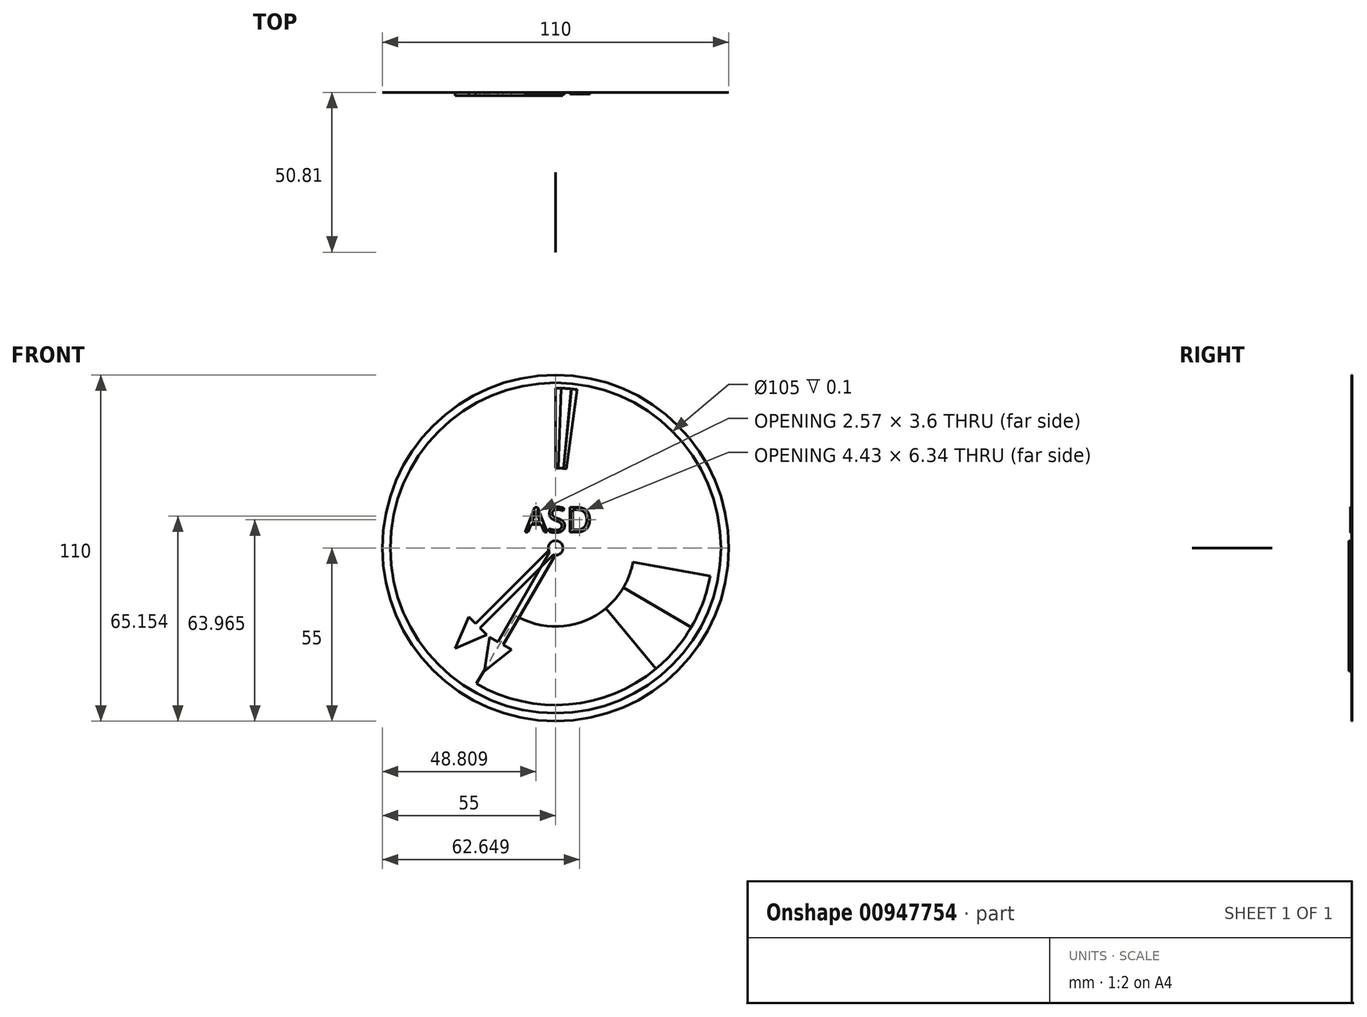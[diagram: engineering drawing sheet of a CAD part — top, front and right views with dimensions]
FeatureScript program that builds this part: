
annotation { "Feature Type Name" : "Feature", "Feature Type Description" : "" }
export const myFeature = defineFeature(function(context is Context, id is Id, definition is map)
    precondition{}
    {
        {
            var Q0;
            Q0=qCreatedBy(makeId("Right.planeOp"),FACE);
            var sketch = newSketch(context, id + "F0", { "sketchPlane" : qUnion([Q0])});
            skLineSegment(sketch, "E0", {"start": v(0, 0) * mm, "end": v(-116.06, 0) * mm, "construction": true});
            skSolve(sketch);
        }
        {
            var Q0;
            Q0=qCreatedBy(makeId("Right.planeOp"),FACE);
            var Q1;
            Q1=sQuery(id+"F0.wireOp",EDGE,"E0");
            cPlane(context, id + "F1", {"entities" : qUnion([Q0, Q1]), "cplaneType" : CPlaneType.LINE_ANGLE, "offset" : 25 * mm, "angle" : 135 * degree, "width" : 150 * mm, "height" : 150 * mm});
        }
        {
            var Q0;
            Q0=qCreatedBy(id+"F1.planeOp",FACE);
            var sketch = newSketch(context, id + "F2", { "sketchPlane" : qUnion([Q0])});
            skLineSegment(sketch, "E1.bottom", {"start": v(-25.4, 0) * mm, "end": v(-50.8, 0) * mm});
            skLineSegment(sketch, "E1.top", {"start": v(-25.4, 0) * mm, "end": v(-50.8, 0) * mm});
            skLineSegment(sketch, "E1.left", {"start": v(-25.4, 0) * mm, "end": v(-25.4, 0) * mm});
            skLineSegment(sketch, "E1.right", {"start": v(-50.8, 0) * mm, "end": v(-50.8, 0) * mm});
            skSolve(sketch);
        }
        {
            var Q0;
            Q0=qSketchRegion(id+"F2",true);
            var Q1;
            Q1=sQuery(id+"F0.wireOp",EDGE,"E0");
            revolve(context, id + "F3", {"surfaceOperationType" : NewSurfaceOperationType.NEW, "entities" : qUnion([Q0]), "axis" : qUnion([Q1]), "revolveType" : RevolveType.ONE_DIRECTION, "oppositeDirection" : true, "angle" : 135 * degree});
        }
        {
            var Q0;
            Q0=qCreatedBy(makeId("Right.planeOp"),FACE);
            var sketch = newSketch(context, id + "F4", { "sketchPlane" : qUnion([Q0])});
            skLineSegment(sketch, "E2.bottom", {"start": v(-0.01, 50.8) * mm, "end": v(0, 50.8) * mm});
            skLineSegment(sketch, "E2.top", {"start": v(0, 25.4) * mm, "end": v(0, 25.4) * mm});
            skLineSegment(sketch, "E2.left", {"start": v(-0.01, 50.8) * mm, "end": v(0, 25.4) * mm});
            skLineSegment(sketch, "E2.right", {"start": v(0, 50.8) * mm, "end": v(0, 25.4) * mm});
            skSolve(sketch);
        }
        {
            var Q0;
            Q0=qSketchRegion(id+"F4",true);
            var Q1;
            Q1=sQuery(id+"F0.wireOp",EDGE,"E0");
            revolve(context, id + "F5", {"surfaceOperationType" : NewSurfaceOperationType.NEW, "entities" : qUnion([Q0]), "axis" : qUnion([Q1]), "revolveType" : RevolveType.ONE_DIRECTION, "oppositeDirection" : true, "angle" : 2 * degree});
        }
        {
            var Q0;
            Q0=qCreatedBy(makeId("Right.planeOp"),FACE);
            var Q1;
            Q1=sQuery(id+"F0.wireOp",EDGE,"E0");
            cPlane(context, id + "F6", {"entities" : qUnion([Q0, Q1]), "cplaneType" : CPlaneType.LINE_ANGLE, "offset" : 25 * mm, "angle" : 2 * degree, "oppositeDirection" : true, "width" : 150 * mm, "height" : 150 * mm});
        }
        {
            var Q0;
            Q0=qCreatedBy(id+"F6.planeOp",FACE);
            var sketch = newSketch(context, id + "F7", { "sketchPlane" : qUnion([Q0])});
            skLineSegment(sketch, "E3.bottom", {"start": v(0, 50.8) * mm, "end": v(0, 50.8) * mm});
            skLineSegment(sketch, "E3.top", {"start": v(0, 25.4) * mm, "end": v(0, 25.4) * mm});
            skLineSegment(sketch, "E3.left", {"start": v(0, 50.8) * mm, "end": v(0, 25.4) * mm});
            skLineSegment(sketch, "E3.right", {"start": v(0, 50.8) * mm, "end": v(0, 25.4) * mm});
            skSolve(sketch);
        }
        {
            var Q0;
            Q0=qSketchRegion(id+"F7",true);
            var Q1;
            Q1=sQuery(id+"F0.wireOp",EDGE,"E0");
            revolve(context, id + "F8", {"surfaceOperationType" : NewSurfaceOperationType.NEW, "entities" : qUnion([Q0]), "axis" : qUnion([Q1]), "revolveType" : RevolveType.ONE_DIRECTION, "oppositeDirection" : true, "angle" : 3.6 * degree});
        }
        {
            var Q0;
            Q0=qCreatedBy(makeId("Front.planeOp"),FACE);
            var sketch = newSketch(context, id + "F9", { "sketchPlane" : qUnion([Q0])});
            skLineSegment(sketch, "E4.bottom", {"start": v(-0.77, -2.19) * mm, "end": v(-24.04, -25.46) * mm});
            skLineSegment(sketch, "E4.top", {"start": v(-2.19, -0.77) * mm, "end": v(-25.46, -24.04) * mm});
            skPoint(sketch, "E4.middle", {"position": v(0, 0) * mm});
            skLineSegment(sketch, "E5", {"start": v(0, 0) * mm, "end": v(0, 10.99) * mm, "construction": true});
            skPoint(sketch, "E6", {"position": v(-24.75, -24.75) * mm});
            skCircle(sketch, "E7", {"center": v(-24.75, -24.75) * mm, "radius": 10.19 * mm, "construction": true});
            skLineSegment(sketch, "E8", {"start": v(-24.04, -25.46) * mm, "end": v(-21.92, -27.58) * mm});
            skLineSegment(sketch, "E9", {"start": v(-25.46, -24.04) * mm, "end": v(-27.58, -21.92) * mm});
            skLineSegment(sketch, "E10", {"start": v(-24.75, -24.75) * mm, "end": v(-31.95, -31.95) * mm, "construction": true});
            skLineSegment(sketch, "E11", {"start": v(-31.95, -31.95) * mm, "end": v(-27.58, -21.92) * mm});
            skLineSegment(sketch, "E12", {"start": v(-21.92, -27.58) * mm, "end": v(-31.95, -31.95) * mm});
            skArc(sketch, "E13", {"start": v(-0.77, -2.19) * mm, "mid": v(1.64, 1.64) * mm, "end": v(-2.19, -0.77) * mm});
            skPoint(sketch, "E14.orphan", {"position": v(-0.7, 0.7) * mm});
            skPoint(sketch, "E15.end.orphan", {"position": v(0.7, -0.7) * mm});
            skSolve(sketch);
        }
        {
            var Q0;
            Q0=qSketchRegion(id+"F9",true);
            extrude(context, id + "F10", {"entities" : qUnion([Q0]), "depth" : 1 * mm, "offsetDistance" : 25 * mm});
        }
        {
            var Q0;
            Q0=qCreatedBy(makeId("Front.planeOp"),FACE);
            var sketch = newSketch(context, id + "F11", { "sketchPlane" : qUnion([Q0])});
            skCircle(sketch, "E16", {"center": v(0, 0) * mm, "radius": 52.5 * mm});
            skCircle(sketch, "E17", {"center": v(0, 0) * mm, "radius": 55 * mm});
            skSolve(sketch);
        }
        {
            var Q0;
            Q0=qSketchRegion(id+"F11",true);
            extrude(context, id + "F12", {"entities" : qUnion([Q0]), "depth" : .1 * mm, "offsetDistance" : 25 * mm});
        }
        {
            var Q0;
            Q0=qCreatedBy(makeId("Front.planeOp"),FACE);
            var sketch = newSketch(context, id + "F13", { "sketchPlane" : qUnion([Q0])});
            skPoint(sketch, "E18.middle", {"position": v(68.26, -76.77) * mm});
            skText(sketch, "E19", { "text": "SPEED", "fontName": "OpenSans-Bold.ttf"});
            skLineSegment(sketch, "E20", {"start": v(0, 0) * mm, "end": v(0, -24.7) * mm, "construction": true});
            const initialGuessF13  = {"E19": [-0.015, -0.03702, 1, 0, 0.007]};
            skSetInitialGuess(sketch, initialGuessF13);
            skSolve(sketch);
        }
        {
            var Q0;
            Q0 = qSketchRegion(id + "F13", true);
            extrude(context, id + "F14", {"entities" : qUnion([Q0]), "depth" : .1 * mm, "offsetDistance" : 25 * mm});
        }
        {
            var Q0;
            Q0=qCreatedBy(makeId("Front.planeOp"),FACE);
            var sketch = newSketch(context, id + "F15", { "sketchPlane" : qUnion([Q0])});
            skLineSegment(sketch, "E21", {"start": v(3.53, 25.15) * mm, "end": v(7.07, 50.3) * mm});
            skLineSegment(sketch, "E22", {"start": v(0, 0) * mm, "end": v(0, 18.46) * mm, "construction": true});
            skArc(sketch, "E23", {"start": v(3.53, 25.15) * mm, "mid": v(3.97, 25.09) * mm, "end": v(4.41, 25.01) * mm});
            skArc(sketch, "E24", {"start": v(7.07, 50.3) * mm, "mid": v(7.95, 50.17) * mm, "end": v(8.82, 50.03) * mm});
            skLineSegment(sketch, "E25", {"start": v(4.41, 25.01) * mm, "end": v(8.82, 50.03) * mm});
            skSolve(sketch);
        }
        {
            var Q0;
            Q0 = qSketchRegion(id + "F15", true);
            extrude(context, id + "F16", {"entities" : qUnion([Q0]), "depth" : .1 * mm, "offsetDistance" : 25 * mm});
        }
        {
            var Q0;
            Q0=makeQuery(id+"F16.opExtrude","SWEPT_BODY",BODY,{"disambiguationData":[OSD([sQuery(id+"F15.wireOp",EDGE,"E21"),sQuery(id+"F15.wireOp",EDGE,"E23"),sQuery(id+"F15.wireOp",EDGE,"E24"),sQuery(id+"F15.wireOp",EDGE,"E25")])]});
            var Q1;
            Q1=makeQuery(id+"F12.opExtrude","CAP_EDGE",EDGE,{"disambiguationData":[OSD([sQuery(id+"F11.wireOp",EDGE,"E16")])],"isStart":false});
            transform(context, id + "F17", {"entities" : qUnion([Q0]), "transformType" : TransformType.ROTATION, "transformAxis" : qUnion([Q1]), "angle" : 2.3 * degree, "makeCopy" : false});
        }
        {
            var Q0;
            Q0=makeQuery(id+"F14.opExtrude","SWEPT_BODY",BODY,{"disambiguationData":[OSD([sQuery(id+"F13.wireOp",EDGE,"E19.sketch_text.stroke-0"),sQuery(id+"F13.wireOp",EDGE,"E19.sketch_text.stroke-1"),sQuery(id+"F13.wireOp",EDGE,"E19.sketch_text.stroke-2"),sQuery(id+"F13.wireOp",EDGE,"E19.sketch_text.stroke-3"),sQuery(id+"F13.wireOp",EDGE,"E19.sketch_text.stroke-4"),sQuery(id+"F13.wireOp",EDGE,"E19.sketch_text.stroke-5"),sQuery(id+"F13.wireOp",EDGE,"E19.sketch_text.stroke-6"),sQuery(id+"F13.wireOp",EDGE,"E19.sketch_text.stroke-7"),sQuery(id+"F13.wireOp",EDGE,"E19.sketch_text.stroke-8"),sQuery(id+"F13.wireOp",EDGE,"E19.sketch_text.stroke-9"),sQuery(id+"F13.wireOp",EDGE,"E19.sketch_text.stroke-10"),sQuery(id+"F13.wireOp",EDGE,"E19.sketch_text.stroke-11"),sQuery(id+"F13.wireOp",EDGE,"E19.sketch_text.stroke-12"),sQuery(id+"F13.wireOp",EDGE,"E19.sketch_text.stroke-13"),sQuery(id+"F13.wireOp",EDGE,"E19.sketch_text.stroke-14"),sQuery(id+"F13.wireOp",EDGE,"E19.sketch_text.stroke-15"),sQuery(id+"F13.wireOp",EDGE,"E19.sketch_text.stroke-16"),sQuery(id+"F13.wireOp",EDGE,"E19.sketch_text.stroke-17"),sQuery(id+"F13.wireOp",EDGE,"E19.sketch_text.stroke-18"),sQuery(id+"F13.wireOp",EDGE,"E19.sketch_text.stroke-19"),sQuery(id+"F13.wireOp",EDGE,"E19.sketch_text.stroke-20"),sQuery(id+"F13.wireOp",EDGE,"E19.sketch_text.stroke-21"),sQuery(id+"F13.wireOp",EDGE,"E19.sketch_text.stroke-22"),sQuery(id+"F13.wireOp",EDGE,"E19.sketch_text.stroke-23"),sQuery(id+"F13.wireOp",EDGE,"E19.sketch_text.stroke-24"),sQuery(id+"F13.wireOp",EDGE,"E19.sketch_text.stroke-25"),sQuery(id+"F13.wireOp",EDGE,"E19.sketch_text.stroke-26"),sQuery(id+"F13.wireOp",EDGE,"E19.sketch_text.stroke-27")])]});
            var Q1;
            Q1=makeQuery(id+"F14.opExtrude","SWEPT_BODY",BODY,{"disambiguationData":[OSD([sQuery(id+"F13.wireOp",EDGE,"E19.sketch_text.stroke-28"),sQuery(id+"F13.wireOp",EDGE,"E19.sketch_text.stroke-29"),sQuery(id+"F13.wireOp",EDGE,"E19.sketch_text.stroke-30"),sQuery(id+"F13.wireOp",EDGE,"E19.sketch_text.stroke-31"),sQuery(id+"F13.wireOp",EDGE,"E19.sketch_text.stroke-32"),sQuery(id+"F13.wireOp",EDGE,"E19.sketch_text.stroke-33"),sQuery(id+"F13.wireOp",EDGE,"E19.sketch_text.stroke-34"),sQuery(id+"F13.wireOp",EDGE,"E19.sketch_text.stroke-35"),sQuery(id+"F13.wireOp",EDGE,"E19.sketch_text.stroke-36"),sQuery(id+"F13.wireOp",EDGE,"E19.sketch_text.stroke-37"),sQuery(id+"F13.wireOp",EDGE,"E19.sketch_text.stroke-38"),sQuery(id+"F13.wireOp",EDGE,"E19.sketch_text.stroke-39"),sQuery(id+"F13.wireOp",EDGE,"E19.sketch_text.stroke-40"),sQuery(id+"F13.wireOp",EDGE,"E19.sketch_text.stroke-41"),sQuery(id+"F13.wireOp",EDGE,"E19.sketch_text.stroke-42"),sQuery(id+"F13.wireOp",EDGE,"E19.sketch_text.stroke-43")])]});
            var Q2;
            Q2=makeQuery(id+"F14.opExtrude","SWEPT_BODY",BODY,{"disambiguationData":[OSD([sQuery(id+"F13.wireOp",EDGE,"E19.sketch_text.stroke-44"),sQuery(id+"F13.wireOp",EDGE,"E19.sketch_text.stroke-45"),sQuery(id+"F13.wireOp",EDGE,"E19.sketch_text.stroke-46"),sQuery(id+"F13.wireOp",EDGE,"E19.sketch_text.stroke-47"),sQuery(id+"F13.wireOp",EDGE,"E19.sketch_text.stroke-48"),sQuery(id+"F13.wireOp",EDGE,"E19.sketch_text.stroke-49"),sQuery(id+"F13.wireOp",EDGE,"E19.sketch_text.stroke-50"),sQuery(id+"F13.wireOp",EDGE,"E19.sketch_text.stroke-51"),sQuery(id+"F13.wireOp",EDGE,"E19.sketch_text.stroke-52"),sQuery(id+"F13.wireOp",EDGE,"E19.sketch_text.stroke-53"),sQuery(id+"F13.wireOp",EDGE,"E19.sketch_text.stroke-54"),sQuery(id+"F13.wireOp",EDGE,"E19.sketch_text.stroke-55")])]});
            var Q3;
            Q3=makeQuery(id+"F14.opExtrude","SWEPT_BODY",BODY,{"disambiguationData":[OSD([sQuery(id+"F13.wireOp",EDGE,"E19.sketch_text.stroke-56"),sQuery(id+"F13.wireOp",EDGE,"E19.sketch_text.stroke-57"),sQuery(id+"F13.wireOp",EDGE,"E19.sketch_text.stroke-58"),sQuery(id+"F13.wireOp",EDGE,"E19.sketch_text.stroke-59"),sQuery(id+"F13.wireOp",EDGE,"E19.sketch_text.stroke-60"),sQuery(id+"F13.wireOp",EDGE,"E19.sketch_text.stroke-61"),sQuery(id+"F13.wireOp",EDGE,"E19.sketch_text.stroke-62"),sQuery(id+"F13.wireOp",EDGE,"E19.sketch_text.stroke-63"),sQuery(id+"F13.wireOp",EDGE,"E19.sketch_text.stroke-64"),sQuery(id+"F13.wireOp",EDGE,"E19.sketch_text.stroke-65"),sQuery(id+"F13.wireOp",EDGE,"E19.sketch_text.stroke-66"),sQuery(id+"F13.wireOp",EDGE,"E19.sketch_text.stroke-67")])]});
            var Q4;
            Q4=makeQuery(id+"F14.opExtrude","SWEPT_BODY",BODY,{"disambiguationData":[OSD([sQuery(id+"F13.wireOp",EDGE,"E19.sketch_text.stroke-68"),sQuery(id+"F13.wireOp",EDGE,"E19.sketch_text.stroke-69"),sQuery(id+"F13.wireOp",EDGE,"E19.sketch_text.stroke-70"),sQuery(id+"F13.wireOp",EDGE,"E19.sketch_text.stroke-71"),sQuery(id+"F13.wireOp",EDGE,"E19.sketch_text.stroke-72"),sQuery(id+"F13.wireOp",EDGE,"E19.sketch_text.stroke-73"),sQuery(id+"F13.wireOp",EDGE,"E19.sketch_text.stroke-74"),sQuery(id+"F13.wireOp",EDGE,"E19.sketch_text.stroke-75"),sQuery(id+"F13.wireOp",EDGE,"E19.sketch_text.stroke-76"),sQuery(id+"F13.wireOp",EDGE,"E19.sketch_text.stroke-77"),sQuery(id+"F13.wireOp",EDGE,"E19.sketch_text.stroke-78"),sQuery(id+"F13.wireOp",EDGE,"E19.sketch_text.stroke-79")])]});
            deleteBodies(context, id + "F18", {"entities" : qUnion([Q0, Q1, Q2, Q3, Q4])});
        }
        {
            var Q0;
            Q0=qCreatedBy(makeId("Front.planeOp"),FACE);
            var sketch = newSketch(context, id + "F19", { "sketchPlane" : qUnion([Q0])});
            skText(sketch, "E26", { "text": "     19\nKts/Sec", "fontName": "OpenSans-Regular.ttf"});
            const initialGuessF19  = {"E26": [0.00712, -0.01436, 1, 0, 0.007]};
            skSetInitialGuess(sketch, initialGuessF19);
            skSolve(sketch);
        }
        {
            var Q0;
            Q0 = qSketchRegion(id + "F19", true);
            extrude(context, id + "F20", {"entities" : qUnion([Q0]), "depth" : 0.5 * mm, "offsetDistance" : 25 * mm});
        }
        {
            var Q0;
            Q0=makeQuery(id+"F20.opExtrude","SWEPT_BODY",BODY,{"disambiguationData":[OSD([sQuery(id+"F19.wireOp",EDGE,"E26.sketch_text.stroke-139"),sQuery(id+"F19.wireOp",EDGE,"E26.sketch_text.stroke-140"),sQuery(id+"F19.wireOp",EDGE,"E26.sketch_text.stroke-141"),sQuery(id+"F19.wireOp",EDGE,"E26.sketch_text.stroke-142"),sQuery(id+"F19.wireOp",EDGE,"E26.sketch_text.stroke-143"),sQuery(id+"F19.wireOp",EDGE,"E26.sketch_text.stroke-144"),sQuery(id+"F19.wireOp",EDGE,"E26.sketch_text.stroke-145"),sQuery(id+"F19.wireOp",EDGE,"E26.sketch_text.stroke-146"),sQuery(id+"F19.wireOp",EDGE,"E26.sketch_text.stroke-147"),sQuery(id+"F19.wireOp",EDGE,"E26.sketch_text.stroke-148"),sQuery(id+"F19.wireOp",EDGE,"E26.sketch_text.stroke-149"),sQuery(id+"F19.wireOp",EDGE,"E26.sketch_text.stroke-150"),sQuery(id+"F19.wireOp",EDGE,"E26.sketch_text.stroke-151"),sQuery(id+"F19.wireOp",EDGE,"E26.sketch_text.stroke-152"),sQuery(id+"F19.wireOp",EDGE,"E26.sketch_text.stroke-153")])]});
            var Q1;
            Q1=makeQuery(id+"F20.opExtrude","SWEPT_BODY",BODY,{"disambiguationData":[OSD([sQuery(id+"F19.wireOp",EDGE,"E26.sketch_text.stroke-120"),sQuery(id+"F19.wireOp",EDGE,"E26.sketch_text.stroke-121"),sQuery(id+"F19.wireOp",EDGE,"E26.sketch_text.stroke-122"),sQuery(id+"F19.wireOp",EDGE,"E26.sketch_text.stroke-123"),sQuery(id+"F19.wireOp",EDGE,"E26.sketch_text.stroke-124"),sQuery(id+"F19.wireOp",EDGE,"E26.sketch_text.stroke-125"),sQuery(id+"F19.wireOp",EDGE,"E26.sketch_text.stroke-126"),sQuery(id+"F19.wireOp",EDGE,"E26.sketch_text.stroke-127"),sQuery(id+"F19.wireOp",EDGE,"E26.sketch_text.stroke-128"),sQuery(id+"F19.wireOp",EDGE,"E26.sketch_text.stroke-129"),sQuery(id+"F19.wireOp",EDGE,"E26.sketch_text.stroke-130"),sQuery(id+"F19.wireOp",EDGE,"E26.sketch_text.stroke-131"),sQuery(id+"F19.wireOp",EDGE,"E26.sketch_text.stroke-132"),sQuery(id+"F19.wireOp",EDGE,"E26.sketch_text.stroke-133"),sQuery(id+"F19.wireOp",EDGE,"E26.sketch_text.stroke-134"),sQuery(id+"F19.wireOp",EDGE,"E26.sketch_text.stroke-135"),sQuery(id+"F19.wireOp",EDGE,"E26.sketch_text.stroke-136"),sQuery(id+"F19.wireOp",EDGE,"E26.sketch_text.stroke-137"),sQuery(id+"F19.wireOp",EDGE,"E26.sketch_text.stroke-138")])]});
            var Q2;
            Q2=makeQuery(id+"F20.opExtrude","SWEPT_BODY",BODY,{"disambiguationData":[OSD([sQuery(id+"F19.wireOp",EDGE,"E26.sketch_text.stroke-95"),sQuery(id+"F19.wireOp",EDGE,"E26.sketch_text.stroke-96"),sQuery(id+"F19.wireOp",EDGE,"E26.sketch_text.stroke-97"),sQuery(id+"F19.wireOp",EDGE,"E26.sketch_text.stroke-98"),sQuery(id+"F19.wireOp",EDGE,"E26.sketch_text.stroke-99"),sQuery(id+"F19.wireOp",EDGE,"E26.sketch_text.stroke-100"),sQuery(id+"F19.wireOp",EDGE,"E26.sketch_text.stroke-101"),sQuery(id+"F19.wireOp",EDGE,"E26.sketch_text.stroke-102"),sQuery(id+"F19.wireOp",EDGE,"E26.sketch_text.stroke-103"),sQuery(id+"F19.wireOp",EDGE,"E26.sketch_text.stroke-104"),sQuery(id+"F19.wireOp",EDGE,"E26.sketch_text.stroke-105"),sQuery(id+"F19.wireOp",EDGE,"E26.sketch_text.stroke-106"),sQuery(id+"F19.wireOp",EDGE,"E26.sketch_text.stroke-107"),sQuery(id+"F19.wireOp",EDGE,"E26.sketch_text.stroke-108"),sQuery(id+"F19.wireOp",EDGE,"E26.sketch_text.stroke-109"),sQuery(id+"F19.wireOp",EDGE,"E26.sketch_text.stroke-110"),sQuery(id+"F19.wireOp",EDGE,"E26.sketch_text.stroke-111"),sQuery(id+"F19.wireOp",EDGE,"E26.sketch_text.stroke-112"),sQuery(id+"F19.wireOp",EDGE,"E26.sketch_text.stroke-113"),sQuery(id+"F19.wireOp",EDGE,"E26.sketch_text.stroke-114"),sQuery(id+"F19.wireOp",EDGE,"E26.sketch_text.stroke-115"),sQuery(id+"F19.wireOp",EDGE,"E26.sketch_text.stroke-116"),sQuery(id+"F19.wireOp",EDGE,"E26.sketch_text.stroke-117"),sQuery(id+"F19.wireOp",EDGE,"E26.sketch_text.stroke-118"),sQuery(id+"F19.wireOp",EDGE,"E26.sketch_text.stroke-119")])]});
            var Q3;
            Q3=makeQuery(id+"F20.opExtrude","SWEPT_BODY",BODY,{"disambiguationData":[OSD([sQuery(id+"F19.wireOp",EDGE,"E26.sketch_text.stroke-91"),sQuery(id+"F19.wireOp",EDGE,"E26.sketch_text.stroke-92"),sQuery(id+"F19.wireOp",EDGE,"E26.sketch_text.stroke-93"),sQuery(id+"F19.wireOp",EDGE,"E26.sketch_text.stroke-94")])]});
            var Q4;
            Q4=makeQuery(id+"F20.opExtrude","SWEPT_BODY",BODY,{"disambiguationData":[OSD([sQuery(id+"F19.wireOp",EDGE,"E26.sketch_text.stroke-66"),sQuery(id+"F19.wireOp",EDGE,"E26.sketch_text.stroke-67"),sQuery(id+"F19.wireOp",EDGE,"E26.sketch_text.stroke-68"),sQuery(id+"F19.wireOp",EDGE,"E26.sketch_text.stroke-69"),sQuery(id+"F19.wireOp",EDGE,"E26.sketch_text.stroke-70"),sQuery(id+"F19.wireOp",EDGE,"E26.sketch_text.stroke-71"),sQuery(id+"F19.wireOp",EDGE,"E26.sketch_text.stroke-72"),sQuery(id+"F19.wireOp",EDGE,"E26.sketch_text.stroke-73"),sQuery(id+"F19.wireOp",EDGE,"E26.sketch_text.stroke-74"),sQuery(id+"F19.wireOp",EDGE,"E26.sketch_text.stroke-75"),sQuery(id+"F19.wireOp",EDGE,"E26.sketch_text.stroke-76"),sQuery(id+"F19.wireOp",EDGE,"E26.sketch_text.stroke-77"),sQuery(id+"F19.wireOp",EDGE,"E26.sketch_text.stroke-78"),sQuery(id+"F19.wireOp",EDGE,"E26.sketch_text.stroke-79"),sQuery(id+"F19.wireOp",EDGE,"E26.sketch_text.stroke-80"),sQuery(id+"F19.wireOp",EDGE,"E26.sketch_text.stroke-81"),sQuery(id+"F19.wireOp",EDGE,"E26.sketch_text.stroke-82"),sQuery(id+"F19.wireOp",EDGE,"E26.sketch_text.stroke-83"),sQuery(id+"F19.wireOp",EDGE,"E26.sketch_text.stroke-84"),sQuery(id+"F19.wireOp",EDGE,"E26.sketch_text.stroke-85"),sQuery(id+"F19.wireOp",EDGE,"E26.sketch_text.stroke-86"),sQuery(id+"F19.wireOp",EDGE,"E26.sketch_text.stroke-87"),sQuery(id+"F19.wireOp",EDGE,"E26.sketch_text.stroke-88"),sQuery(id+"F19.wireOp",EDGE,"E26.sketch_text.stroke-89"),sQuery(id+"F19.wireOp",EDGE,"E26.sketch_text.stroke-90")])]});
            var Q5;
            Q5=makeQuery(id+"F20.opExtrude","SWEPT_BODY",BODY,{"disambiguationData":[OSD([sQuery(id+"F19.wireOp",EDGE,"E26.sketch_text.stroke-47"),sQuery(id+"F19.wireOp",EDGE,"E26.sketch_text.stroke-48"),sQuery(id+"F19.wireOp",EDGE,"E26.sketch_text.stroke-49"),sQuery(id+"F19.wireOp",EDGE,"E26.sketch_text.stroke-50"),sQuery(id+"F19.wireOp",EDGE,"E26.sketch_text.stroke-51"),sQuery(id+"F19.wireOp",EDGE,"E26.sketch_text.stroke-52"),sQuery(id+"F19.wireOp",EDGE,"E26.sketch_text.stroke-53"),sQuery(id+"F19.wireOp",EDGE,"E26.sketch_text.stroke-54"),sQuery(id+"F19.wireOp",EDGE,"E26.sketch_text.stroke-55"),sQuery(id+"F19.wireOp",EDGE,"E26.sketch_text.stroke-56"),sQuery(id+"F19.wireOp",EDGE,"E26.sketch_text.stroke-57"),sQuery(id+"F19.wireOp",EDGE,"E26.sketch_text.stroke-58"),sQuery(id+"F19.wireOp",EDGE,"E26.sketch_text.stroke-59"),sQuery(id+"F19.wireOp",EDGE,"E26.sketch_text.stroke-60"),sQuery(id+"F19.wireOp",EDGE,"E26.sketch_text.stroke-61"),sQuery(id+"F19.wireOp",EDGE,"E26.sketch_text.stroke-62"),sQuery(id+"F19.wireOp",EDGE,"E26.sketch_text.stroke-63"),sQuery(id+"F19.wireOp",EDGE,"E26.sketch_text.stroke-64"),sQuery(id+"F19.wireOp",EDGE,"E26.sketch_text.stroke-65")])]});
            var Q6;
            Q6=makeQuery(id+"F20.opExtrude","SWEPT_BODY",BODY,{"disambiguationData":[OSD([sQuery(id+"F19.wireOp",EDGE,"E26.sketch_text.stroke-35"),sQuery(id+"F19.wireOp",EDGE,"E26.sketch_text.stroke-36"),sQuery(id+"F19.wireOp",EDGE,"E26.sketch_text.stroke-37"),sQuery(id+"F19.wireOp",EDGE,"E26.sketch_text.stroke-38"),sQuery(id+"F19.wireOp",EDGE,"E26.sketch_text.stroke-39"),sQuery(id+"F19.wireOp",EDGE,"E26.sketch_text.stroke-40"),sQuery(id+"F19.wireOp",EDGE,"E26.sketch_text.stroke-41"),sQuery(id+"F19.wireOp",EDGE,"E26.sketch_text.stroke-42"),sQuery(id+"F19.wireOp",EDGE,"E26.sketch_text.stroke-43"),sQuery(id+"F19.wireOp",EDGE,"E26.sketch_text.stroke-44"),sQuery(id+"F19.wireOp",EDGE,"E26.sketch_text.stroke-45"),sQuery(id+"F19.wireOp",EDGE,"E26.sketch_text.stroke-46")])]});
            var Q7;
            Q7=makeQuery(id+"F20.opExtrude","SWEPT_BODY",BODY,{"disambiguationData":[OSD([sQuery(id+"F19.wireOp",EDGE,"E26.sketch_text.stroke-9"),sQuery(id+"F19.wireOp",EDGE,"E26.sketch_text.stroke-10"),sQuery(id+"F19.wireOp",EDGE,"E26.sketch_text.stroke-11"),sQuery(id+"F19.wireOp",EDGE,"E26.sketch_text.stroke-12"),sQuery(id+"F19.wireOp",EDGE,"E26.sketch_text.stroke-13"),sQuery(id+"F19.wireOp",EDGE,"E26.sketch_text.stroke-14"),sQuery(id+"F19.wireOp",EDGE,"E26.sketch_text.stroke-15"),sQuery(id+"F19.wireOp",EDGE,"E26.sketch_text.stroke-16"),sQuery(id+"F19.wireOp",EDGE,"E26.sketch_text.stroke-17"),sQuery(id+"F19.wireOp",EDGE,"E26.sketch_text.stroke-18"),sQuery(id+"F19.wireOp",EDGE,"E26.sketch_text.stroke-19"),sQuery(id+"F19.wireOp",EDGE,"E26.sketch_text.stroke-20"),sQuery(id+"F19.wireOp",EDGE,"E26.sketch_text.stroke-21"),sQuery(id+"F19.wireOp",EDGE,"E26.sketch_text.stroke-22"),sQuery(id+"F19.wireOp",EDGE,"E26.sketch_text.stroke-23"),sQuery(id+"F19.wireOp",EDGE,"E26.sketch_text.stroke-24"),sQuery(id+"F19.wireOp",EDGE,"E26.sketch_text.stroke-25"),sQuery(id+"F19.wireOp",EDGE,"E26.sketch_text.stroke-26"),sQuery(id+"F19.wireOp",EDGE,"E26.sketch_text.stroke-27"),sQuery(id+"F19.wireOp",EDGE,"E26.sketch_text.stroke-28"),sQuery(id+"F19.wireOp",EDGE,"E26.sketch_text.stroke-29"),sQuery(id+"F19.wireOp",EDGE,"E26.sketch_text.stroke-30"),sQuery(id+"F19.wireOp",EDGE,"E26.sketch_text.stroke-31"),sQuery(id+"F19.wireOp",EDGE,"E26.sketch_text.stroke-32"),sQuery(id+"F19.wireOp",EDGE,"E26.sketch_text.stroke-33"),sQuery(id+"F19.wireOp",EDGE,"E26.sketch_text.stroke-34")])]});
            var Q8;
            Q8=makeQuery(id+"F20.opExtrude","SWEPT_BODY",BODY,{"disambiguationData":[OSD([sQuery(id+"F19.wireOp",EDGE,"E26.sketch_text.stroke-0"),sQuery(id+"F19.wireOp",EDGE,"E26.sketch_text.stroke-1"),sQuery(id+"F19.wireOp",EDGE,"E26.sketch_text.stroke-2"),sQuery(id+"F19.wireOp",EDGE,"E26.sketch_text.stroke-3"),sQuery(id+"F19.wireOp",EDGE,"E26.sketch_text.stroke-4"),sQuery(id+"F19.wireOp",EDGE,"E26.sketch_text.stroke-5"),sQuery(id+"F19.wireOp",EDGE,"E26.sketch_text.stroke-6"),sQuery(id+"F19.wireOp",EDGE,"E26.sketch_text.stroke-7"),sQuery(id+"F19.wireOp",EDGE,"E26.sketch_text.stroke-8")])]});
            deleteBodies(context, id + "F21", {"entities" : qUnion([Q0, Q1, Q2, Q3, Q4, Q5, Q6, Q7, Q8])});
        }
        {
            var Q0;
            Q0=qCreatedBy(makeId("Front.planeOp"),FACE);
            var sketch = newSketch(context, id + "F22", { "sketchPlane" : qUnion([Q0])});
            skLineSegment(sketch, "E27", {"start": v(0, 0) * mm, "end": v(-25.14, -43.08) * mm, "construction": true});
            skLineSegment(sketch, "E28", {"start": v(-25.14, -43.08) * mm, "end": v(-12.57, -21.54) * mm});
            skSolve(sketch);
        }
        {
            var Q0;
            Q0=sQuery(id+"F22.wireOp",EDGE,"E28");
            cPlane(context, id + "F23", {"entities" : qUnion([Q0]), "cplaneType" : CPlaneType.LINE_ANGLE, "offset" : 25 * mm, "angle" : 0 * degree, "width" : 150 * mm, "height" : 150 * mm});
        }
        {
            var Q0;
            Q0=qCreatedBy(id+"F23.planeOp",FACE);
            var sketch = newSketch(context, id + "F24", { "sketchPlane" : qUnion([Q0])});
            skLineSegment(sketch, "E29.bottom", {"start": v(0, -24.94) * mm, "end": v(0.01, -24.94) * mm});
            skLineSegment(sketch, "E29.top", {"start": v(0, -49.88) * mm, "end": v(0.01, -49.88) * mm});
            skLineSegment(sketch, "E29.left", {"start": v(0, -24.94) * mm, "end": v(0, -49.88) * mm});
            skLineSegment(sketch, "E29.right", {"start": v(0.01, -24.94) * mm, "end": v(0.01, -49.88) * mm});
            skSolve(sketch);
        }
        {
            var Q0;
            Q0 = qSketchRegion(id + "F24", true);
            var Q1;
            Q1=makeQuery(id+"F12.opExtrude","CAP_EDGE",EDGE,{"disambiguationData":[OSD([sQuery(id+"F11.wireOp",EDGE,"E16")])],"isStart":false});
            revolve(context, id + "F25", {"surfaceOperationType" : NewSurfaceOperationType.NEW, "entities" : qUnion([Q0]), "axis" : qUnion([Q1]), "revolveType" : RevolveType.ONE_DIRECTION, "angle" : 70 * degree});
        }
        {
            var Q0;
            Q0 = qSketchRegion(id + "F24", true);
            var Q1;
            Q1=makeQuery(id+"F12.opExtrude","CAP_EDGE",EDGE,{"disambiguationData":[OSD([sQuery(id+"F11.wireOp",EDGE,"E16")])],"isStart":false});
            revolve(context, id + "F26", {"operationType" : NewBodyOperationType.ADD, "surfaceOperationType" : NewSurfaceOperationType.NEW, "entities" : qUnion([Q0]), "axis" : qUnion([Q1]), "revolveType" : RevolveType.ONE_DIRECTION, "angle" : 10 * degree});
        }
        {
            var Q0;
            Q0 = qSketchRegion(id + "F24", true);
            var Q1;
            Q1=makeQuery(id+"F12.opExtrude","CAP_EDGE",EDGE,{"disambiguationData":[OSD([sQuery(id+"F11.wireOp",EDGE,"E17")])],"isStart":false});
            revolve(context, id + "F27", {"surfaceOperationType" : NewSurfaceOperationType.NEW, "entities" : qUnion([Q0]), "axis" : qUnion([Q1]), "revolveType" : RevolveType.ONE_DIRECTION, "angle" : 20 * degree});
        }
        {
            var Q0;
            Q0=makeQuery(id+"F27.opRevolve","SWEPT_BODY",BODY,{"disambiguationData":[OSD([sQuery(id+"F24.wireOp",EDGE,"E29.bottom"),sQuery(id+"F24.wireOp",EDGE,"E29.top"),sQuery(id+"F24.wireOp",EDGE,"E29.left"),sQuery(id+"F24.wireOp",EDGE,"E29.right")])]});
            var Q1;
            Q1=makeQuery(id+"F12.opExtrude","CAP_EDGE",EDGE,{"disambiguationData":[OSD([sQuery(id+"F11.wireOp",EDGE,"E16")])],"isStart":false});
            transform(context, id + "F28", {"entities" : qUnion([Q0]), "transformType" : TransformType.ROTATION, "transformAxis" : qUnion([Q1]), "angle" : 90 * degree, "makeCopy" : false});
        }
        {
            var Q0;
            Q0 = qSketchRegion(id + "F24", true);
            var Q1;
            Q1=makeQuery(id+"F12.opExtrude","CAP_EDGE",EDGE,{"disambiguationData":[OSD([sQuery(id+"F11.wireOp",EDGE,"E16")])],"isStart":false});
            revolve(context, id + "F29", {"operationType" : NewBodyOperationType.ADD, "surfaceOperationType" : NewSurfaceOperationType.NEW, "entities" : qUnion([Q0]), "axis" : qUnion([Q1]), "revolveType" : RevolveType.ONE_DIRECTION, "angle" : 15 * degree});
        }
        {
            var Q0;
            Q0 = qSketchRegion(id + "F24", true);
            var Q1;
            Q1=makeQuery(id+"F12.opExtrude","CAP_EDGE",EDGE,{"disambiguationData":[OSD([sQuery(id+"F11.wireOp",EDGE,"E17")])],"isStart":false});
            revolve(context, id + "F30", {"surfaceOperationType" : NewSurfaceOperationType.NEW, "entities" : qUnion([Q0]), "axis" : qUnion([Q1]), "revolveType" : RevolveType.ONE_DIRECTION, "angle" : 20 * degree});
        }
        {
            var Q0;
            Q0=makeQuery(id+"F30.opRevolve","SWEPT_BODY",BODY,{"disambiguationData":[OSD([sQuery(id+"F24.wireOp",EDGE,"E29.bottom"),sQuery(id+"F24.wireOp",EDGE,"E29.top"),sQuery(id+"F24.wireOp",EDGE,"E29.left"),sQuery(id+"F24.wireOp",EDGE,"E29.right")])]});
            var Q1;
            Q1=makeQuery(id+"F12.opExtrude","CAP_EDGE",EDGE,{"disambiguationData":[OSD([sQuery(id+"F11.wireOp",EDGE,"E17")])],"isStart":false});
            transform(context, id + "F31", {"entities" : qUnion([Q0]), "transformType" : TransformType.ROTATION, "transformAxis" : qUnion([Q1]), "angle" : 70 * degree, "makeCopy" : false});
        }
        {
            var Q0;
            Q0=makeQuery(id+"F10.opExtrude","SWEPT_BODY",BODY,{"disambiguationData":[OSD([sQuery(id+"F9.wireOp",EDGE,"E4.bottom"),sQuery(id+"F9.wireOp",EDGE,"E4.top"),sQuery(id+"F9.wireOp",EDGE,"E8"),sQuery(id+"F9.wireOp",EDGE,"E9"),sQuery(id+"F9.wireOp",EDGE,"E11"),sQuery(id+"F9.wireOp",EDGE,"E12"),sQuery(id+"F9.wireOp",EDGE,"E13")])]});
            transform(context, id + "F32", {"entities" : qUnion([Q0]), "transformType" : TransformType.TRANSLATION_3D, "dx" : 0 * mm, "dy" : 0 * mm, "dz" : 0 * mm, "makeCopy" : true});
        }
        {
            var Q0;
            Q0=makeQuery(id+"F32.opPattern","COPY",BODY,{"derivedFrom":makeQuery(id+"F10.opExtrude","SWEPT_BODY",BODY,{"disambiguationData":[OSD([sQuery(id+"F9.wireOp",EDGE,"E4.bottom"),sQuery(id+"F9.wireOp",EDGE,"E4.top"),sQuery(id+"F9.wireOp",EDGE,"E8"),sQuery(id+"F9.wireOp",EDGE,"E9"),sQuery(id+"F9.wireOp",EDGE,"E11"),sQuery(id+"F9.wireOp",EDGE,"E12"),sQuery(id+"F9.wireOp",EDGE,"E13")])]}),"instanceName":"1"});
            var Q1;
            Q1=makeQuery(id+"F12.opExtrude","CAP_EDGE",EDGE,{"disambiguationData":[OSD([sQuery(id+"F11.wireOp",EDGE,"E17")])],"isStart":false});
            transform(context, id + "F33", {"entities" : qUnion([Q0]), "transformType" : TransformType.ROTATION, "transformAxis" : qUnion([Q1]), "angle" : 15 * degree, "makeCopy" : false});
        }
        {
            var Q0;
            Q0=qCreatedBy(makeId("Front.planeOp"),FACE);
            var sketch = newSketch(context, id + "F34", { "sketchPlane" : qUnion([Q0])});
            skLineSegment(sketch, "E30", {"start": v(0, 0) * mm, "end": v(-42.47, -42.38) * mm, "construction": true});
            skSolve(sketch);
        }
        {
            var Q0;
            Q0=sQuery(id+"F34.wireOp",EDGE,"E30");
            cPlane(context, id + "F35", {"entities" : qUnion([Q0]), "cplaneType" : CPlaneType.LINE_ANGLE, "offset" : 25 * mm, "angle" : 90 * degree, "width" : 150 * mm, "height" : 150 * mm});
        }
        {
            var Q0;
            Q0=qCreatedBy(makeId("Front.planeOp"),FACE);
            var sketch = newSketch(context, id + "F36", { "sketchPlane" : qUnion([Q0])});
            skLineSegment(sketch, "E31", {"start": v(0, 0) * mm, "end": v(-30.23, -51.83) * mm, "construction": true});
            skSolve(sketch);
        }
        {
            var Q0;
            Q0=sQuery(id+"F36.wireOp",EDGE,"E31");
            cPlane(context, id + "F37", {"entities" : qUnion([Q0]), "cplaneType" : CPlaneType.LINE_ANGLE, "offset" : 25 * mm, "angle" : 0 * degree, "width" : 150 * mm, "height" : 150 * mm});
        }
        {
            var Q0;
            Q0=qCreatedBy(makeId("Front.planeOp"),FACE);
            var sketch = newSketch(context, id + "F38", { "sketchPlane" : qUnion([Q0])});
            skText(sketch, "E32", { "text": "ASD", "fontName": "OpenSans-Regular.ttf"});
            const initialGuessF38  = {"E32": [-0.00971, 0.005, 1, 0, 0.008]};
            skSetInitialGuess(sketch, initialGuessF38);
            skSolve(sketch);
        }
        {
            var Q0;
            Q0 = qSketchRegion(id + "F38", true);
            extrude(context, id + "F39", {"entities" : qUnion([Q0]), "depth" : 0.5 * mm, "offsetDistance" : 25 * mm});
        }
    });
